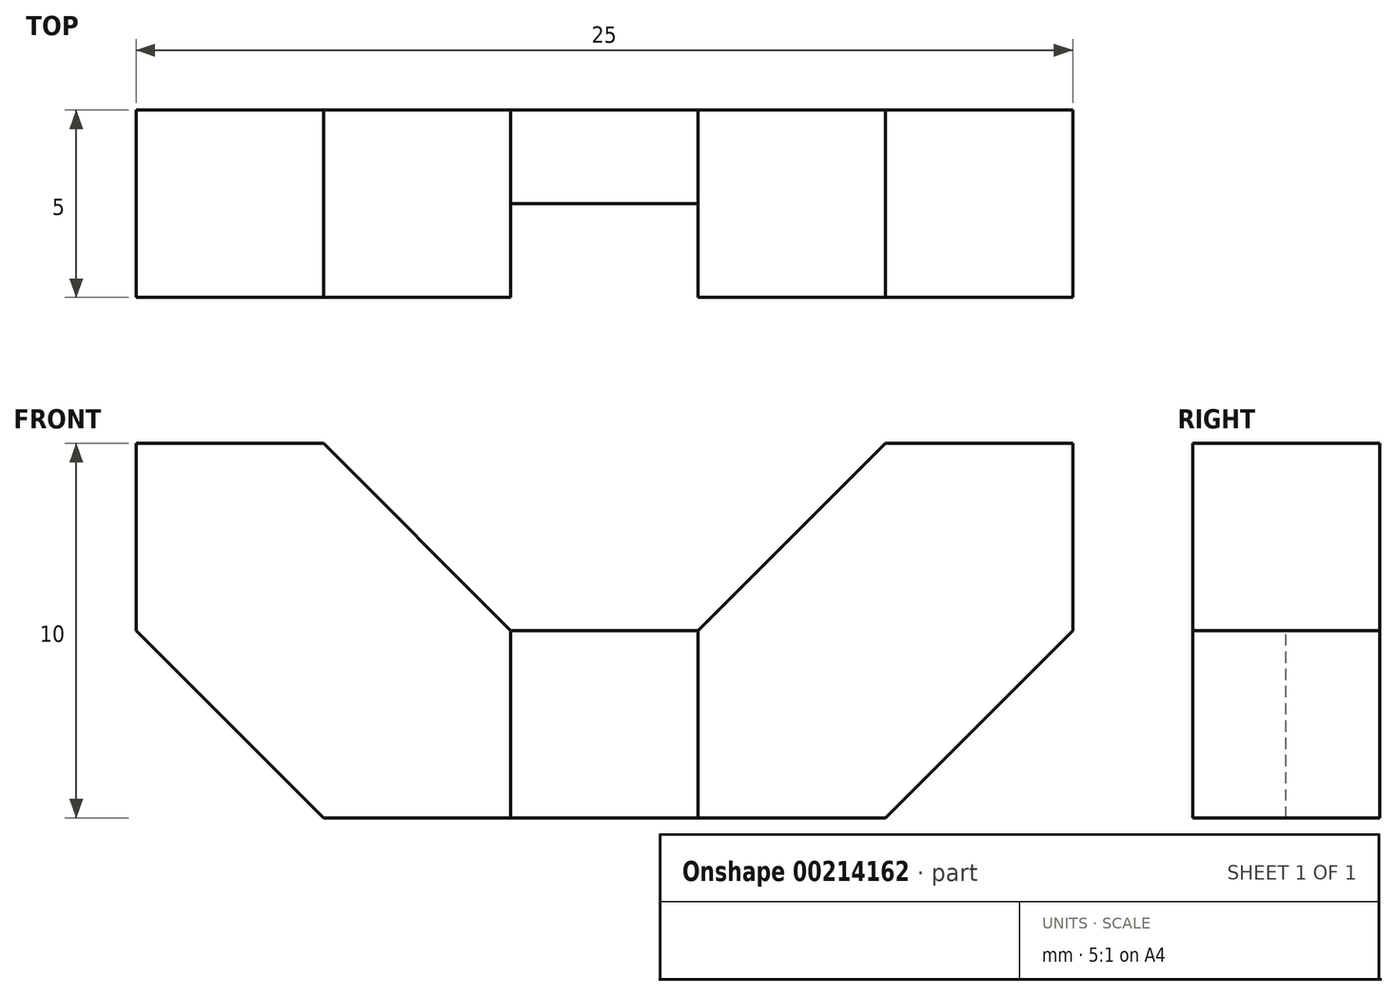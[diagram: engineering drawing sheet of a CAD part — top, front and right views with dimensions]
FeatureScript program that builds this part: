
annotation { "Feature Type Name" : "Feature", "Feature Type Description" : "" }
export const myFeature = defineFeature(function(context is Context, id is Id, definition is map)
    precondition{}
    {
        {
            var Q0;
            Q0=qCreatedBy(makeId("Front.planeOp"),FACE);
            var sketch = newSketch(context, id + "F0", { "sketchPlane" : qUnion([Q0])});
            skLineSegment(sketch, "E0", {"start": v(0, 0) * mm, "end": v(7.5, 0) * mm});
            skLineSegment(sketch, "E1", {"start": v(7.5, 0) * mm, "end": v(12.5, 5) * mm});
            skLineSegment(sketch, "E2", {"start": v(12.5, 5) * mm, "end": v(12.5, 10) * mm});
            skLineSegment(sketch, "E3", {"start": v(12.5, 10) * mm, "end": v(7.5, 10) * mm});
            skLineSegment(sketch, "E4", {"start": v(7.5, 10) * mm, "end": v(2.5, 5) * mm});
            skLineSegment(sketch, "E5", {"start": v(2.5, 5) * mm, "end": v(0, 5) * mm});
            skLineSegment(sketch, "E6.MirrorCS", {"start": v(-2.5, 5) * mm, "end": v(0, 5) * mm});
            skLineSegment(sketch, "E7.MirrorCS", {"start": v(-7.5, 10) * mm, "end": v(-2.5, 5) * mm});
            skLineSegment(sketch, "E8.MirrorCS", {"start": v(-12.5, 10) * mm, "end": v(-7.5, 10) * mm});
            skLineSegment(sketch, "E9.MirrorCS", {"start": v(-12.5, 5) * mm, "end": v(-12.5, 10) * mm});
            skLineSegment(sketch, "E10.MirrorCS", {"start": v(-7.5, 0) * mm, "end": v(-12.5, 5) * mm});
            skLineSegment(sketch, "E11.MirrorCS", {"start": v(0, 0) * mm, "end": v(-7.5, 0) * mm});
            skSolve(sketch);
        }
        {
            var Q0;
            Q0 = qSketchRegion(id + "F0", true);
            extrude(context, id + "F1", {"entities" : qUnion([Q0]), "endBound" : BoundingType.SYMMETRIC, "depth" : 5 * mm});
        }
        {
            var Q0;
            Q0=qCreatedBy(makeId("Front.planeOp"),FACE);
            var sketch = newSketch(context, id + "F2", { "sketchPlane" : qUnion([Q0])});
            skLineSegment(sketch, "E12.bottom", {"start": v(0, 0) * mm, "end": v(2.5, 0) * mm});
            skLineSegment(sketch, "E12.top", {"start": v(0, 5) * mm, "end": v(2.5, 5) * mm});
            skLineSegment(sketch, "E12.left", {"start": v(0, 0) * mm, "end": v(0, 5) * mm});
            skLineSegment(sketch, "E12.right", {"start": v(2.5, 0) * mm, "end": v(2.5, 5) * mm});
            skLineSegment(sketch, "E13.MirrorCS", {"start": v(0, 0) * mm, "end": v(-2.5, 0) * mm});
            skLineSegment(sketch, "E14.MirrorCS", {"start": v(-2.5, 0) * mm, "end": v(-2.5, 5) * mm});
            skLineSegment(sketch, "E15.MirrorCS", {"start": v(0, 5) * mm, "end": v(-2.5, 5) * mm});
            skSolve(sketch);
        }
        {
            var Q0;
            Q0 = qSketchRegion(id + "F2", true);
            extrude(context, id + "F3", {"entities" : qUnion([Q0]), "operationType" : NewBodyOperationType.REMOVE, "depth" : 10 * mm});
        }
    });
